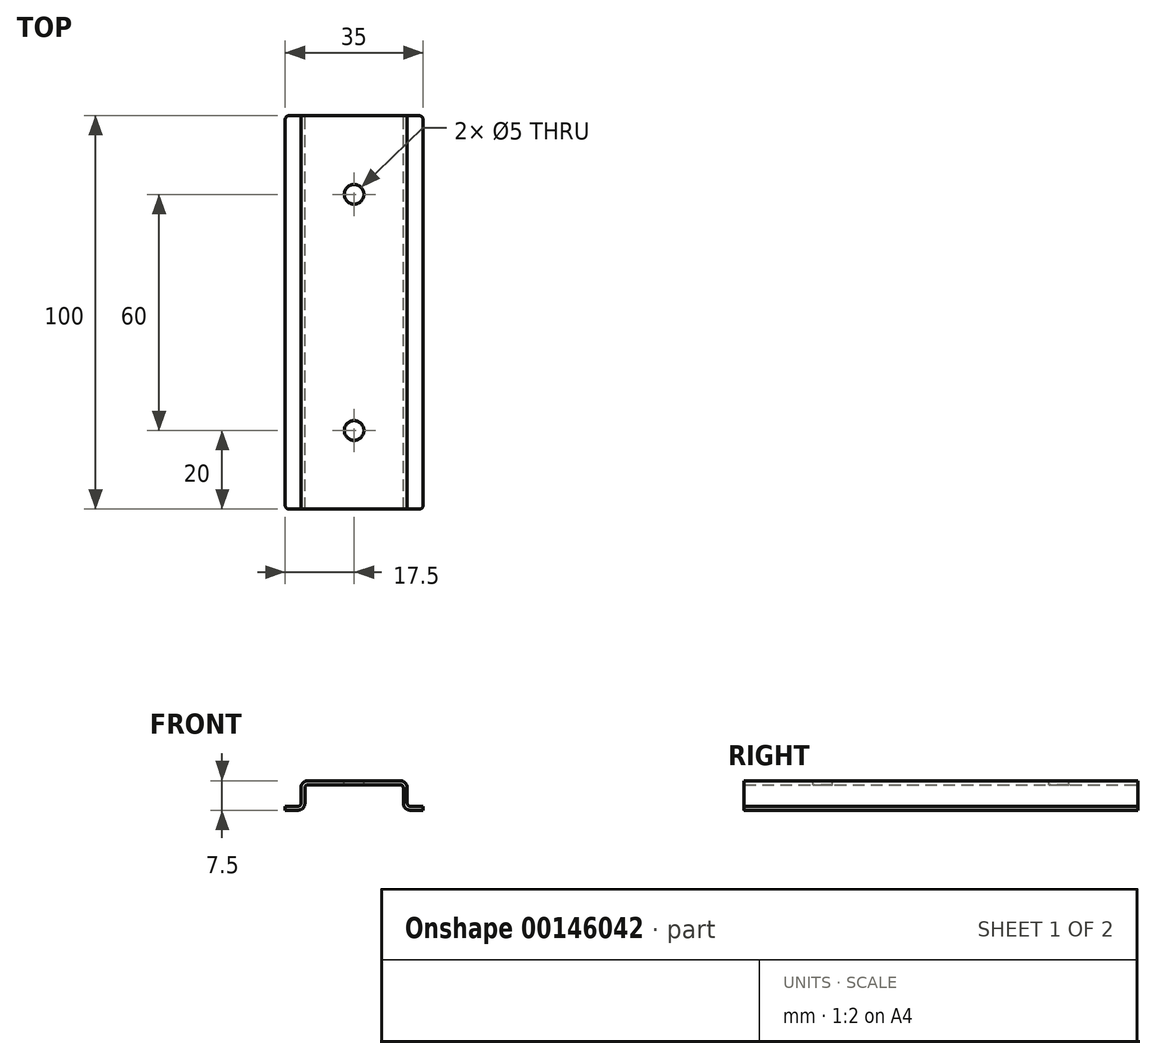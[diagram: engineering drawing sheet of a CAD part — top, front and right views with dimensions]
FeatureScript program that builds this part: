
annotation { "Feature Type Name" : "Feature", "Feature Type Description" : "" }
export const myFeature = defineFeature(function(context is Context, id is Id, definition is map)
    precondition{}
    {
        {
            var Q0;
            Q0=qCreatedBy(makeId("Front.planeOp"),FACE);
            var sketch = newSketch(context, id + "F0", { "sketchPlane" : qUnion([Q0])});
            skLineSegment(sketch, "E0", {"start": v(0, 0) * mm, "end": v(0, 7.5) * mm, "construction": true});
            skLineSegment(sketch, "E1", {"start": v(0, 7.5) * mm, "end": v(-11.7, 7.5) * mm});
            skLineSegment(sketch, "E2", {"start": v(-13.5, 5.7) * mm, "end": v(-13.5, 1.8) * mm});
            skLineSegment(sketch, "E3", {"start": v(-14.3, 1) * mm, "end": v(-17.5, 1) * mm});
            skLineSegment(sketch, "E4", {"start": v(-17.5, 1) * mm, "end": v(-17.5, 0) * mm});
            skLineSegment(sketch, "E5", {"start": v(-17.5, 0) * mm, "end": v(-14.3, 0) * mm});
            skLineSegment(sketch, "E6", {"start": v(-12.5, 1.8) * mm, "end": v(-12.5, 5.7) * mm});
            skLineSegment(sketch, "E7", {"start": v(-11.7, 6.5) * mm, "end": v(0, 6.5) * mm});
            skLineSegment(sketch, "E8.MirrorCS", {"start": v(17.5, 1) * mm, "end": v(17.5, 0) * mm});
            skLineSegment(sketch, "E9.MirrorCS", {"start": v(0, 7.5) * mm, "end": v(11.7, 7.5) * mm});
            skLineSegment(sketch, "E10.MirrorCS", {"start": v(13.5, 5.7) * mm, "end": v(13.5, 1.8) * mm});
            skLineSegment(sketch, "E11.MirrorCS", {"start": v(17.5, 0) * mm, "end": v(14.3, 0) * mm});
            skLineSegment(sketch, "E12.MirrorCS", {"start": v(12.5, 1.8) * mm, "end": v(12.5, 5.7) * mm});
            skLineSegment(sketch, "E13.MirrorCS", {"start": v(14.3, 1) * mm, "end": v(17.5, 1) * mm});
            skLineSegment(sketch, "E14.MirrorCS", {"start": v(11.7, 6.5) * mm, "end": v(0, 6.5) * mm});
            skPoint(sketch, "E15.visualSharp", {"position": v(-12.5, 6.5) * mm});
            skArc(sketch, "E15.filletArc", {"start": v(-11.7, 6.5) * mm, "mid": v(-12.27, 6.27) * mm, "end": v(-12.5, 5.7) * mm});
            skPoint(sketch, "E16.visualSharp", {"position": v(12.5, 6.5) * mm});
            skArc(sketch, "E16.filletArc", {"start": v(12.5, 5.7) * mm, "mid": v(12.27, 6.27) * mm, "end": v(11.7, 6.5) * mm});
            skPoint(sketch, "E17.visualSharp", {"position": v(13.5, 1) * mm});
            skArc(sketch, "E17.filletArc", {"start": v(13.5, 1.8) * mm, "mid": v(13.73, 1.23) * mm, "end": v(14.3, 1) * mm});
            skPoint(sketch, "E18.visualSharp", {"position": v(-13.5, 1) * mm});
            skArc(sketch, "E18.filletArc", {"start": v(-14.3, 1) * mm, "mid": v(-13.73, 1.23) * mm, "end": v(-13.5, 1.8) * mm});
            skPoint(sketch, "E19.visualSharp", {"position": v(-13.5, 7.5) * mm});
            skArc(sketch, "E19.filletArc", {"start": v(-11.7, 7.5) * mm, "mid": v(-12.97, 6.97) * mm, "end": v(-13.5, 5.7) * mm});
            skPoint(sketch, "E20.visualSharp", {"position": v(13.5, 7.5) * mm});
            skArc(sketch, "E20.filletArc", {"start": v(13.5, 5.7) * mm, "mid": v(12.97, 6.97) * mm, "end": v(11.7, 7.5) * mm});
            skPoint(sketch, "E21.visualSharp", {"position": v(12.5, 0) * mm});
            skArc(sketch, "E21.filletArc", {"start": v(12.5, 1.8) * mm, "mid": v(13.03, 0.53) * mm, "end": v(14.3, 0) * mm});
            skPoint(sketch, "E22.visualSharp", {"position": v(-12.5, 0) * mm});
            skArc(sketch, "E22.filletArc", {"start": v(-14.3, 0) * mm, "mid": v(-13.03, 0.53) * mm, "end": v(-12.5, 1.8) * mm});
            skSolve(sketch);
        }
        {
            var Q0;
            Q0=qSketchRegion(id+"F0",true);
            extrude(context, id + "F1", {"entities" : qUnion([Q0]), "endBound" : BoundingType.SYMMETRIC, "depth" : 100 * mm});
        }
        {
            var Q0;
            Q0=makeQuery(id+"F1.opExtrude","SWEPT_FACE",FACE,{"disambiguationData":[OSD([sQuery(id+"F0.wireOp",EDGE,"E1"),sQuery(id+"F0.wireOp",EDGE,"E9.MirrorCS")])]});
            var sketch = newSketch(context, id + "F2", { "sketchPlane" : qUnion([Q0])});
            skCircle(sketch, "E23", {"center": v(0, 30) * mm, "radius": 2.5 * mm});
            skPoint(sketch, "E23.centerSnap0", {"position": v(0, 50) * mm});
            skCircle(sketch, "E24", {"center": v(0, -30) * mm, "radius": 2.5 * mm});
            skPoint(sketch, "E24.centerSnap0", {"position": v(0, -50) * mm});
            skSolve(sketch);
        }
        {
            var Q0;
            Q0=makeQuery(id+"F2.imprint","IMPRINT",FACE,{"disambiguationData":[TD([[makeQuery(id+"F2.imprint","IMPRINT",EDGE,{"derivedFrom":sQuery(id+"F2.wireOp",EDGE,"E23")}),1.0]])]});
            var Q1;
            Q1=makeQuery(id+"F2.imprint","IMPRINT",FACE,{"disambiguationData":[TD([[makeQuery(id+"F2.imprint","IMPRINT",EDGE,{"derivedFrom":sQuery(id+"F2.wireOp",EDGE,"E24")}),1.0]])]});
            extrude(context, id + "F3", {"entities" : qUnion([Q0, Q1]), "operationType" : NewBodyOperationType.REMOVE, "oppositeDirection" : true, "depth" : 25 * mm});
        }
        {
            var Q0;
            Q0=makeQuery(id+"F1.opExtrude","CAP_EDGE",EDGE,{"disambiguationData":[OSD([sQuery(id+"F0.wireOp",EDGE,"E8.MirrorCS")])],"isStart":true});
            var Q1;
            Q1=makeQuery(id+"F1.opExtrude","CAP_EDGE",EDGE,{"disambiguationData":[OSD([sQuery(id+"F0.wireOp",EDGE,"E4")])],"isStart":true});
            var Q2;
            Q2=makeQuery(id+"F1.opExtrude","CAP_EDGE",EDGE,{"disambiguationData":[OSD([sQuery(id+"F0.wireOp",EDGE,"E8.MirrorCS")])],"isStart":false});
            var Q3;
            Q3=makeQuery(id+"F1.opExtrude","CAP_EDGE",EDGE,{"disambiguationData":[OSD([sQuery(id+"F0.wireOp",EDGE,"E4")])],"isStart":false});
            fillet(context, id + "F4", {"entities" : qUnion([Q0, Q1, Q2, Q3]), "radius" : 1 * mm, "tangentPropagation" : true, "allowEdgeOverflow" : false});
        }
    });
